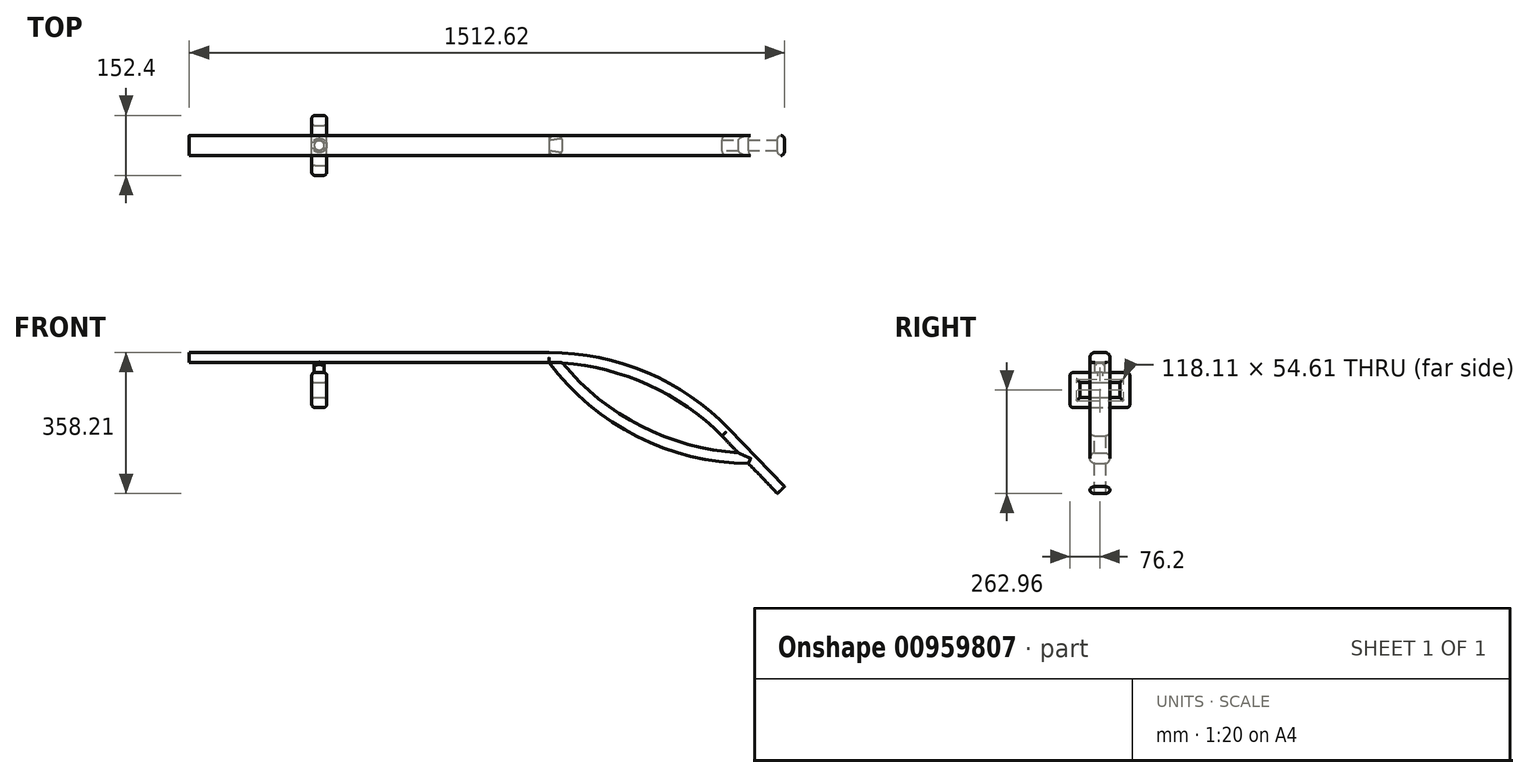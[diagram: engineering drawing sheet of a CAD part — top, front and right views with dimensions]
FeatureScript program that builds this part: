
annotation { "Feature Type Name" : "Feature", "Feature Type Description" : "" }
export const myFeature = defineFeature(function(context is Context, id is Id, definition is map)
    precondition{}
    {
        {
            var Q0;
            Q0=qCreatedBy(makeId("Right.planeOp"),FACE);
            var sketch = newSketch(context, id + "F0", { "sketchPlane" : qUnion([Q0])});
            skLineSegment(sketch, "E0.bottom", {"start": v(12.7, 12.7) * mm, "end": v(-12.7, 12.7) * mm});
            skLineSegment(sketch, "E0.top", {"start": v(12.7, -12.7) * mm, "end": v(-12.7, -12.7) * mm});
            skLineSegment(sketch, "E0.left", {"start": v(12.7, 12.7) * mm, "end": v(12.7, -12.7) * mm});
            skLineSegment(sketch, "E0.right", {"start": v(-12.7, 12.7) * mm, "end": v(-12.7, -12.7) * mm});
            skPoint(sketch, "E0.middle", {"position": v(0, 0) * mm});
            skCircle(sketch, "E1", {"center": v(12.7, 0) * mm, "radius": 12.7 * mm});
            skCircle(sketch, "E2", {"center": v(-12.7, 0) * mm, "radius": 12.7 * mm});
            skSolve(sketch);
        }
        {
            var Q0;
            {var subQ0=sQuery(id+"F0.wireOp",EDGE,"E0.right");Q0=makeQuery(id+"F0.imprint","IMPRINT",FACE,{"disambiguationData":[TD([[makeQuery(id+"F0.imprint","IMPRINT",EDGE,{"derivedFrom":subQ0}),-1.0]])]});}
            var Q1;
            {var subQ0=sQuery(id+"F0.wireOp",EDGE,"E0.right");Q1=makeQuery(id+"F0.imprint","IMPRINT",FACE,{"disambiguationData":[TD([[makeQuery(id+"F0.imprint","IMPRINT",EDGE,{"derivedFrom":subQ0}),1.0]])]});}
            var Q2;
            {var subQ0=sQuery(id+"F0.wireOp",EDGE,"E0.bottom");Q2=makeQuery(id+"F0.imprint","IMPRINT",FACE,{"disambiguationData":[TD([[makeQuery(id+"F0.imprint","IMPRINT",EDGE,{"derivedFrom":subQ0}),1.0]])]});}
            var Q3;
            {var subQ0=sQuery(id+"F0.wireOp",EDGE,"E0.left");Q3=makeQuery(id+"F0.imprint","IMPRINT",FACE,{"disambiguationData":[TD([[makeQuery(id+"F0.imprint","IMPRINT",EDGE,{"derivedFrom":subQ0}),-1.0]])]});}
            var Q4;
            {var subQ0=sQuery(id+"F0.wireOp",EDGE,"E0.top");Q4=makeQuery(id+"F0.imprint","IMPRINT",FACE,{"disambiguationData":[TD([[makeQuery(id+"F0.imprint","IMPRINT",EDGE,{"derivedFrom":subQ0}),-1.0]])]});}
            var Q5;
            {var subQ0=sQuery(id+"F0.wireOp",EDGE,"E0.left");Q5=makeQuery(id+"F0.imprint","IMPRINT",FACE,{"disambiguationData":[TD([[makeQuery(id+"F0.imprint","IMPRINT",EDGE,{"derivedFrom":subQ0}),1.0]])]});}
            extrude(context, id + "F1", {"entities" : qUnion([Q0, Q1, Q2, Q3, Q4, Q5]), "depth" : 457.2 * mm, "offsetDistance" : 25.4 * mm, "hasSecondDirection" : true, "secondDirectionOppositeDirection" : true, "secondDirectionDepth" : 457.2 * mm});
        }
        {
            var Q0;
            Q0=qCreatedBy(makeId("Front.planeOp"),FACE);
            var sketch = newSketch(context, id + "F2", { "sketchPlane" : qUnion([Q0])});
            skArc(sketch, "E3", {"start": v(914.4, -181.63) * mm, "mid": v(705.6, -37.9) * mm, "end": v(457.2, 12.7) * mm});
            skLineSegment(sketch, "E4.bottom", {"start": v(0, 0) * mm, "end": v(457.2, 0) * mm});
            skLineSegment(sketch, "E4.top", {"start": v(0, 12.7) * mm, "end": v(457.2, 12.7) * mm});
            skLineSegment(sketch, "E4.left", {"start": v(0, 0) * mm, "end": v(0, 12.7) * mm});
            skLineSegment(sketch, "E4.right", {"start": v(457.2, 0) * mm, "end": v(457.2, 12.7) * mm});
            skLineSegment(sketch, "E5", {"start": v(914.4, -181.63) * mm, "end": v(896.11, -199.25) * mm});
            skLineSegment(sketch, "E6", {"start": v(457.2, 12.7) * mm, "end": v(457.2, -12.7) * mm});
            skArc(sketch, "E7", {"start": v(914.4, -218.38) * mm, "mid": v(706.96, -68.5) * mm, "end": v(457.2, -12.7) * mm});
            skSolve(sketch);
        }
        {
            var Q0;
            {var subQ0=sQuery(id+"F2.wireOp",EDGE,"E3");Q0=makeQuery(id+"F2.imprint","IMPRINT",FACE,{"disambiguationData":[TD([[makeQuery(id+"F2.imprint","IMPRINT",EDGE,{"derivedFrom":subQ0}),1.0]])]});}
            extrude(context, id + "F3", {"entities" : qUnion([Q0]), "depth" : 25.4 * mm, "offsetDistance" : 25.4 * mm, "hasSecondDirection" : true, "secondDirectionOppositeDirection" : true, "secondDirectionDepth" : 25.4 * mm});
        }
        {
            var Q0;
            Q0=makeQuery(id+"F3.opExtrude","CAP_EDGE",EDGE,{"disambiguationData":[OSD([sQuery(id+"F2.wireOp",EDGE,"E3")])],"isStart":false});
            var Q1;
            Q1=makeQuery(id+"F3.opExtrude","CAP_EDGE",EDGE,{"disambiguationData":[OSD([sQuery(id+"F2.wireOp",EDGE,"E7")])],"isStart":false});
            var Q2;
            Q2=makeQuery(id+"F3.opExtrude","CAP_EDGE",EDGE,{"disambiguationData":[OSD([sQuery(id+"F2.wireOp",EDGE,"E7")])],"isStart":true});
            var Q3;
            Q3=makeQuery(id+"F3.opExtrude","CAP_EDGE",EDGE,{"disambiguationData":[OSD([sQuery(id+"F2.wireOp",EDGE,"E3")])],"isStart":true});
            fillet(context, id + "F4", {"entities" : qUnion([Q0, Q1, Q2, Q3]), "radius" : 12.7 * mm, "tangentPropagation" : true, "allowEdgeOverflow" : false});
        }
        {
            var Q0;
            Q0=qCreatedBy(makeId("Front.planeOp"),FACE);
            var sketch = newSketch(context, id + "F5", { "sketchPlane" : qUnion([Q0])});
            skLineSegment(sketch, "E8.bottom", {"start": v(0, 0) * mm, "end": v(457.2, 0) * mm});
            skLineSegment(sketch, "E8.top", {"start": v(0, 12.7) * mm, "end": v(457.2, 12.7) * mm});
            skLineSegment(sketch, "E8.left", {"start": v(0, 0) * mm, "end": v(0, 12.7) * mm});
            skLineSegment(sketch, "E8.right", {"start": v(457.2, 0) * mm, "end": v(457.2, 12.7) * mm});
            skLineSegment(sketch, "E9", {"start": v(457.2, 0) * mm, "end": v(457.2, -12.7) * mm});
            skArc(sketch, "E10", {"start": v(457.2, -12.7) * mm, "mid": v(684.69, -202.91) * mm, "end": v(973.74, -269.1) * mm});
            skLineSegment(sketch, "E11", {"start": v(457.2, -12.7) * mm, "end": v(641.99, -12.7) * mm});
            skLineSegment(sketch, "E12", {"start": v(457.2, -12.7) * mm, "end": v(477.6, 2.44) * mm});
            skArc(sketch, "E13", {"start": v(477.6, 2.44) * mm, "mid": v(697.42, -177.57) * mm, "end": v(973.74, -243.7) * mm});
            skLineSegment(sketch, "E14", {"start": v(973.74, -243.7) * mm, "end": v(973.5, -269.1) * mm});
            skLineSegment(sketch, "E15", {"start": v(973.74, -269.1) * mm, "end": v(963.6, -243.52) * mm});
            skSolve(sketch);
        }
        {
            var Q0;
            {var subQ3=sQuery(id+"F5.wireOp",EDGE,"E15");var subQ7=sQuery(id+"F5.wireOp",EDGE,"E13");var subQ9=makeQuery(id+"F5.imprint","INTERSECT",VERTEX,{"derivedFrom":[subQ7,subQ3]});Q0=makeQuery(id+"F5.imprint","IMPRINT",FACE,{"disambiguationData":[TD([[makeQuery(id+"F5.imprint","IMPRINT",EDGE,{"disambiguationData":[TD([[subQ9,1.0]])],"derivedFrom":subQ7}),-1.0]])]});}
            extrude(context, id + "F6", {"entities" : qUnion([Q0]), "operationType" : NewBodyOperationType.ADD, "depth" : 25.4 * mm, "offsetDistance" : 25.4 * mm, "hasSecondDirection" : true, "secondDirectionOppositeDirection" : true, "secondDirectionDepth" : 25.4 * mm});
        }
        {
            var Q0;
            Q0=makeQuery(id+"F6.opExtrude","CAP_EDGE",EDGE,{"disambiguationData":[OSD([sQuery(id+"F5.wireOp",EDGE,"E10")])],"isStart":false});
            var Q1;
            Q1=makeQuery(id+"F6.opExtrude","CAP_EDGE",EDGE,{"disambiguationData":[OSD([sQuery(id+"F5.wireOp",EDGE,"E13")])],"isStart":false});
            var Q2;
            Q2=makeQuery(id+"F6.opExtrude","CAP_EDGE",EDGE,{"disambiguationData":[OSD([sQuery(id+"F5.wireOp",EDGE,"E13")])],"isStart":true});
            var Q3;
            Q3=makeQuery(id+"F6.opExtrude","CAP_EDGE",EDGE,{"disambiguationData":[OSD([sQuery(id+"F5.wireOp",EDGE,"E10")])],"isStart":true});
            fillet(context, id + "F7", {"entities" : qUnion([Q0, Q1, Q2, Q3]), "radius" : 12.7 * mm, "tangentPropagation" : true, "allowEdgeOverflow" : false});
        }
        {
            var Q0;
            Q0=makeQuery(id+"F3.opExtrude","SWEPT_FACE",FACE,{"disambiguationData":[OSD([sQuery(id+"F2.wireOp",EDGE,"E5")])]});
            var sketch = newSketch(context, id + "F8", { "sketchPlane" : qUnion([Q0])});
            skLineSegment(sketch, "E16.bottom", {"start": v(532.4, 25.4) * mm, "end": v(507, 25.4) * mm});
            skLineSegment(sketch, "E16.top", {"start": v(532.4, -25.4) * mm, "end": v(507, -25.4) * mm});
            skLineSegment(sketch, "E16.left", {"start": v(532.4, 25.4) * mm, "end": v(532.4, -25.4) * mm});
            skLineSegment(sketch, "E16.right", {"start": v(507, 25.4) * mm, "end": v(507, -25.4) * mm});
            skSolve(sketch);
        }
        {
            var Q0;
            {var subQ0=sQuery(id+"F2.wireOp",EDGE,"E5");var subQ2=sQuery(id+"F2.wireOp",EDGE,"E3");Q0=makeQuery(id+"F8.imprint","IMPRINT",FACE,{"disambiguationData":[TD([[makeQuery(id+"F8.imprint","IMPRINT",EDGE,{"derivedFrom":makeQuery(id+"F3.opExtrude","SWEPT_EDGE",EDGE,{"disambiguationData":[OSD([subQ2,subQ0])]})}),-1.0]])]});}
            extrude(context, id + "F9", {"entities" : qUnion([Q0]), "operationType" : NewBodyOperationType.ADD, "depth" : 203.2 * mm, "offsetDistance" : 25.4 * mm});
        }
        {
            var Q0;
            Q0=makeQuery(id+"F1.opExtrude","SWEPT_FACE",FACE,{"disambiguationData":[OSD([sQuery(id+"F0.wireOp",EDGE,"E0.top")])]});
            var sketch = newSketch(context, id + "F10", { "sketchPlane" : qUnion([Q0])});
            skLineSegment(sketch, "E17", {"start": v(-457.2, 0) * mm, "end": v(-127, 0) * mm});
            skPoint(sketch, "E18.middle", {"position": v(-127, 0) * mm});
            skCircle(sketch, "E19", {"center": v(-127, 0) * mm, "radius": 12.7 * mm});
            skSolve(sketch);
        }
        {
            var Q0;
            {var subQ0=sQuery(id+"F10.wireOp",EDGE,"E19");var subQ1=makeQuery(id+"F10.imprint","INTERSECT",VERTEX,{"derivedFrom":[sQuery(id+"F10.wireOp",EDGE,"E17"),subQ0]});Q0=makeQuery(id+"F10.imprint","IMPRINT",FACE,{"disambiguationData":[TD([[makeQuery(id+"F10.imprint","IMPRINT",EDGE,{"disambiguationData":[TD([[subQ1,1.0]])],"derivedFrom":subQ0}),1.0]])]});}
            extrude(context, id + "F11", {"entities" : qUnion([Q0]), "operationType" : NewBodyOperationType.ADD, "depth" : 25.4 * mm, "offsetDistance" : 25.4 * mm});
        }
        {
            var Q0;
            Q0=makeQuery(id+"F11.boolean.opBoolean","SPLIT",EDGE,{"disambiguationData":[OD(0.0)],"derivedFrom":makeQuery(id+"F11.opExtrude","CAP_EDGE",EDGE,{"disambiguationData":[OSD([sQuery(id+"F10.wireOp",EDGE,"E19")])],"isStart":true})});
            var Q1;
            Q1=makeQuery(id+"F11.boolean.opBoolean","SPLIT",EDGE,{"disambiguationData":[OD(1.0)],"derivedFrom":makeQuery(id+"F11.opExtrude","CAP_EDGE",EDGE,{"disambiguationData":[OSD([sQuery(id+"F10.wireOp",EDGE,"E19")])],"isStart":true})});
            fillet(context, id + "F12", {"entities" : qUnion([Q0, Q1]), "radius" : 6.35 * mm, "tangentPropagation" : true, "allowEdgeOverflow" : false});
        }
        {
            var Q0;
            Q0=makeQuery(id+"F11.opExtrude","CAP_FACE",FACE,{"disambiguationData":[OSD([sQuery(id+"F10.wireOp",EDGE,"E19")])],"isStart":false});
            var sketch = newSketch(context, id + "F13", { "sketchPlane" : qUnion([Q0])});
            skLineSegment(sketch, "E20.bottom", {"start": v(-107.95, 76.2) * mm, "end": v(-146.05, 76.2) * mm});
            skLineSegment(sketch, "E20.top", {"start": v(-107.95, -76.2) * mm, "end": v(-146.05, -76.2) * mm});
            skLineSegment(sketch, "E20.left", {"start": v(-107.95, 76.2) * mm, "end": v(-107.95, -76.2) * mm});
            skLineSegment(sketch, "E20.right", {"start": v(-146.05, 76.2) * mm, "end": v(-146.05, -76.2) * mm});
            skPoint(sketch, "E20.middle", {"position": v(-127, 0) * mm});
            skSolve(sketch);
        }
        {
            var Q0;
            Q0=makeQuery(id+"F13.imprint","IMPRINT",FACE,{"disambiguationData":[TD([[makeQuery(id+"F13.imprint","IMPRINT",EDGE,{"derivedFrom":sQuery(id+"F13.wireOp",EDGE,"E20.bottom")}),1.0]])]});
            var Q1;
            Q1=makeQuery(id+"F13.imprint","IMPRINT",FACE,{"disambiguationData":[TD([[makeQuery(id+"F13.imprint","IMPRINT",EDGE,{"derivedFrom":makeQuery(id+"F11.opExtrude","CAP_EDGE",EDGE,{"disambiguationData":[OSD([sQuery(id+"F10.wireOp",EDGE,"E19")])],"isStart":false})}),1.0]])]});
            extrude(context, id + "F14", {"entities" : qUnion([Q0, Q1]), "operationType" : NewBodyOperationType.ADD, "depth" : 25.4 * mm, "offsetDistance" : 25.4 * mm});
        }
        {
            var Q0;
            Q0=makeQuery(id+"F14.opExtrude","CAP_FACE",FACE,{"disambiguationData":[OSD([sQuery(id+"F13.wireOp",EDGE,"E20.bottom"),sQuery(id+"F13.wireOp",EDGE,"E20.top"),sQuery(id+"F13.wireOp",EDGE,"E20.left"),sQuery(id+"F13.wireOp",EDGE,"E20.right")])],"isStart":false});
            var sketch = newSketch(context, id + "F15", { "sketchPlane" : qUnion([Q0])});
            skLineSegment(sketch, "E21.bottom", {"start": v(-146.05, -76.2) * mm, "end": v(-107.95, -76.2) * mm});
            skLineSegment(sketch, "E21.top", {"start": v(-146.05, -50.8) * mm, "end": v(-107.95, -50.8) * mm});
            skLineSegment(sketch, "E21.left", {"start": v(-146.05, -76.2) * mm, "end": v(-146.05, -50.8) * mm});
            skLineSegment(sketch, "E21.right", {"start": v(-107.95, -76.2) * mm, "end": v(-107.95, -50.8) * mm});
            skLineSegment(sketch, "E22.bottom", {"start": v(-146.05, 76.2) * mm, "end": v(-107.95, 76.2) * mm});
            skLineSegment(sketch, "E22.top", {"start": v(-146.05, 50.8) * mm, "end": v(-107.95, 50.8) * mm});
            skLineSegment(sketch, "E22.left", {"start": v(-146.05, 76.2) * mm, "end": v(-146.05, 50.8) * mm});
            skLineSegment(sketch, "E22.right", {"start": v(-107.95, 76.2) * mm, "end": v(-107.95, 50.8) * mm});
            skSolve(sketch);
        }
        {
            var Q0;
            Q0=makeQuery(id+"F15.imprint","IMPRINT",FACE,{"disambiguationData":[TD([[makeQuery(id+"F15.imprint","IMPRINT",EDGE,{"derivedFrom":sQuery(id+"F15.wireOp",EDGE,"E21.bottom")}),-1.0]])]});
            var Q1;
            Q1=makeQuery(id+"F15.imprint","IMPRINT",FACE,{"disambiguationData":[TD([[makeQuery(id+"F15.imprint","IMPRINT",EDGE,{"derivedFrom":sQuery(id+"F15.wireOp",EDGE,"E22.bottom")}),1.0]])]});
            extrude(context, id + "F16", {"entities" : qUnion([Q0, Q1]), "operationType" : NewBodyOperationType.ADD, "depth" : 38.1 * mm, "offsetDistance" : 25.4 * mm});
        }
        {
            var Q0;
            Q0=makeQuery(id+"F16.opExtrude","CAP_FACE",FACE,{"disambiguationData":[OSD([sQuery(id+"F15.wireOp",EDGE,"E21.bottom"),sQuery(id+"F15.wireOp",EDGE,"E21.top"),sQuery(id+"F15.wireOp",EDGE,"E21.left"),sQuery(id+"F15.wireOp",EDGE,"E21.right")])],"isStart":false});
            var sketch = newSketch(context, id + "F17", { "sketchPlane" : qUnion([Q0])});
            skLineSegment(sketch, "E23.bottom", {"start": v(-146.05, -76.2) * mm, "end": v(-107.95, -76.2) * mm});
            skLineSegment(sketch, "E23.top", {"start": v(-146.05, 76.2) * mm, "end": v(-107.95, 76.2) * mm});
            skLineSegment(sketch, "E23.left", {"start": v(-146.05, -76.2) * mm, "end": v(-146.05, 76.2) * mm});
            skLineSegment(sketch, "E23.right", {"start": v(-107.95, -76.2) * mm, "end": v(-107.95, 76.2) * mm});
            skSolve(sketch);
        }
        {
            var Q0;
            {var subQ0=sQuery(id+"F17.wireOp",EDGE,"E23.bottom");Q0=makeQuery(id+"F17.imprint","IMPRINT",FACE,{"disambiguationData":[TD([[makeQuery(id+"F17.imprint","IMPRINT",EDGE,{"derivedFrom":subQ0}),-1.0]])]});}
            var Q1;
            {var subQ0=sQuery(id+"F17.wireOp",EDGE,"E23.top");Q1=makeQuery(id+"F17.imprint","IMPRINT",FACE,{"disambiguationData":[TD([[makeQuery(id+"F17.imprint","IMPRINT",EDGE,{"derivedFrom":subQ0}),-1.0]])]});}
            extrude(context, id + "F18", {"entities" : qUnion([Q0, Q1]), "operationType" : NewBodyOperationType.ADD, "depth" : 25.4 * mm, "offsetDistance" : 25.4 * mm});
        }
        {
            var Q0;
            Q0=makeQuery(id+"F18.boolean.opBoolean","MERGE",EDGE,{"derivedFrom":[makeQuery(id+"F16.boolean.opBoolean","MERGE",EDGE,{"derivedFrom":[makeQuery(id+"F14.opExtrude","SWEPT_EDGE",EDGE,{"disambiguationData":[OSD([sQuery(id+"F13.wireOp",EDGE,"E20.top"),sQuery(id+"F13.wireOp",EDGE,"E20.right")])]}),makeQuery(id+"F16.opExtrude","SWEPT_EDGE",EDGE,{"disambiguationData":[OSD([sQuery(id+"F15.wireOp",EDGE,"E21.bottom"),sQuery(id+"F15.wireOp",EDGE,"E21.left")])]})]}),makeQuery(id+"F18.opExtrude","SWEPT_EDGE",EDGE,{"disambiguationData":[OSD([sQuery(id+"F17.wireOp",EDGE,"E23.bottom"),sQuery(id+"F17.wireOp",EDGE,"E23.left")])]})]});
            var Q1;
            Q1=makeQuery(id+"F16.opExtrude","SWEPT_EDGE",EDGE,{"disambiguationData":[OSD([sQuery(id+"F13.wireOp",EDGE,"E20.right"),sQuery(id+"F15.wireOp",EDGE,"E21.top"),sQuery(id+"F15.wireOp",EDGE,"E21.left")])]});
            var Q2;
            Q2=makeQuery(id+"F14.opExtrude","CAP_EDGE",EDGE,{"disambiguationData":[OSD([sQuery(id+"F13.wireOp",EDGE,"E20.left")])],"isStart":false});
            var Q3;
            Q3=makeQuery(id+"F18.opExtrude","CAP_EDGE",EDGE,{"disambiguationData":[OSD([sQuery(id+"F17.wireOp",EDGE,"E23.left")])],"isStart":false});
            var Q4;
            Q4=makeQuery(id+"F18.opExtrude","CAP_EDGE",EDGE,{"disambiguationData":[OSD([sQuery(id+"F17.wireOp",EDGE,"E23.bottom")])],"isStart":false});
            var Q5;
            Q5=makeQuery(id+"F18.opExtrude","CAP_EDGE",EDGE,{"disambiguationData":[OSD([sQuery(id+"F17.wireOp",EDGE,"E23.right")])],"isStart":false});
            var Q6;
            Q6=makeQuery(id+"F18.opExtrude","CAP_EDGE",EDGE,{"disambiguationData":[OSD([sQuery(id+"F17.wireOp",EDGE,"E23.right")])],"isStart":true});
            var Q7;
            Q7=makeQuery(id+"F16.opExtrude","SWEPT_EDGE",EDGE,{"disambiguationData":[OSD([sQuery(id+"F13.wireOp",EDGE,"E20.left"),sQuery(id+"F15.wireOp",EDGE,"E21.top"),sQuery(id+"F15.wireOp",EDGE,"E21.right")])]});
            var Q8;
            Q8=makeQuery(id+"F18.boolean.opBoolean","MERGE",EDGE,{"derivedFrom":[makeQuery(id+"F16.boolean.opBoolean","MERGE",EDGE,{"derivedFrom":[makeQuery(id+"F14.opExtrude","SWEPT_EDGE",EDGE,{"disambiguationData":[OSD([sQuery(id+"F13.wireOp",EDGE,"E20.top"),sQuery(id+"F13.wireOp",EDGE,"E20.left")])]}),makeQuery(id+"F16.opExtrude","SWEPT_EDGE",EDGE,{"disambiguationData":[OSD([sQuery(id+"F15.wireOp",EDGE,"E21.bottom"),sQuery(id+"F15.wireOp",EDGE,"E21.right")])]})]}),makeQuery(id+"F18.opExtrude","SWEPT_EDGE",EDGE,{"disambiguationData":[OSD([sQuery(id+"F17.wireOp",EDGE,"E23.bottom"),sQuery(id+"F17.wireOp",EDGE,"E23.right")])]})]});
            var Q9;
            Q9=makeQuery(id+"F18.boolean.opBoolean","MERGE",EDGE,{"derivedFrom":[makeQuery(id+"F16.boolean.opBoolean","MERGE",EDGE,{"derivedFrom":[makeQuery(id+"F14.opExtrude","SWEPT_EDGE",EDGE,{"disambiguationData":[OSD([sQuery(id+"F13.wireOp",EDGE,"E20.bottom"),sQuery(id+"F13.wireOp",EDGE,"E20.left")])]}),makeQuery(id+"F16.opExtrude","SWEPT_EDGE",EDGE,{"disambiguationData":[OSD([sQuery(id+"F15.wireOp",EDGE,"E22.bottom"),sQuery(id+"F15.wireOp",EDGE,"E22.right")])]})]}),makeQuery(id+"F18.opExtrude","SWEPT_EDGE",EDGE,{"disambiguationData":[OSD([sQuery(id+"F17.wireOp",EDGE,"E23.top"),sQuery(id+"F17.wireOp",EDGE,"E23.right")])]})]});
            var Q10;
            Q10=makeQuery(id+"F18.boolean.opBoolean","MERGE",EDGE,{"derivedFrom":[makeQuery(id+"F16.boolean.opBoolean","MERGE",EDGE,{"derivedFrom":[makeQuery(id+"F14.opExtrude","SWEPT_EDGE",EDGE,{"disambiguationData":[OSD([sQuery(id+"F13.wireOp",EDGE,"E20.bottom"),sQuery(id+"F13.wireOp",EDGE,"E20.right")])]}),makeQuery(id+"F16.opExtrude","SWEPT_EDGE",EDGE,{"disambiguationData":[OSD([sQuery(id+"F15.wireOp",EDGE,"E22.bottom"),sQuery(id+"F15.wireOp",EDGE,"E22.left")])]})]}),makeQuery(id+"F18.opExtrude","SWEPT_EDGE",EDGE,{"disambiguationData":[OSD([sQuery(id+"F17.wireOp",EDGE,"E23.top"),sQuery(id+"F17.wireOp",EDGE,"E23.left")])]})]});
            var Q11;
            Q11=makeQuery(id+"F18.opExtrude","CAP_EDGE",EDGE,{"disambiguationData":[OSD([sQuery(id+"F17.wireOp",EDGE,"E23.top")])],"isStart":false});
            var Q12;
            Q12=makeQuery(id+"F14.opExtrude","CAP_EDGE",EDGE,{"disambiguationData":[OSD([sQuery(id+"F13.wireOp",EDGE,"E20.bottom")])],"isStart":true});
            var Q13;
            Q13=makeQuery(id+"F14.opExtrude","CAP_EDGE",EDGE,{"disambiguationData":[OSD([sQuery(id+"F13.wireOp",EDGE,"E20.left")])],"isStart":true});
            var Q14;
            Q14=makeQuery(id+"F14.opExtrude","CAP_EDGE",EDGE,{"disambiguationData":[OSD([sQuery(id+"F13.wireOp",EDGE,"E20.right")])],"isStart":true});
            var Q15;
            Q15=makeQuery(id+"F14.opExtrude","CAP_EDGE",EDGE,{"disambiguationData":[OSD([sQuery(id+"F13.wireOp",EDGE,"E20.top")])],"isStart":true});
            var Q16;
            Q16=makeQuery(id+"F14.opExtrude","CAP_EDGE",EDGE,{"disambiguationData":[OSD([sQuery(id+"F13.wireOp",EDGE,"E20.right")])],"isStart":false});
            var Q17;
            Q17=makeQuery(id+"F16.opExtrude","SWEPT_EDGE",EDGE,{"disambiguationData":[OSD([sQuery(id+"F13.wireOp",EDGE,"E20.right"),sQuery(id+"F15.wireOp",EDGE,"E22.top"),sQuery(id+"F15.wireOp",EDGE,"E22.left")])]});
            var Q18;
            Q18=makeQuery(id+"F18.opExtrude","CAP_EDGE",EDGE,{"disambiguationData":[OSD([sQuery(id+"F17.wireOp",EDGE,"E23.left")])],"isStart":true});
            var Q19;
            Q19=makeQuery(id+"F16.opExtrude","SWEPT_EDGE",EDGE,{"disambiguationData":[OSD([sQuery(id+"F13.wireOp",EDGE,"E20.left"),sQuery(id+"F15.wireOp",EDGE,"E22.top"),sQuery(id+"F15.wireOp",EDGE,"E22.right")])]});
            fillet(context, id + "F19", {"entities" : qUnion([Q0, Q1, Q2, Q3, Q4, Q5, Q6, Q7, Q8, Q9, Q10, Q11, Q12, Q13, Q14, Q15, Q16, Q17, Q18, Q19]), "radius" : 8.25 * mm, "tangentPropagation" : true, "allowEdgeOverflow" : false});
        }
    });
